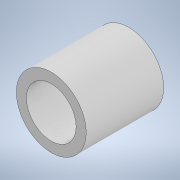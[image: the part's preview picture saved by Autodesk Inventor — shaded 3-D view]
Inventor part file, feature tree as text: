
AUTODESK INVENTOR PART (.ipt)
format: ipt  version: 2020 (Build 240168000, 168)  size: 101,888 bytes
history: native  units: in
note: dims shown in document units (in); Inventor stores cm internally (conversion verified against a paired STEP export)
features: extrude x1
ambient origin geometry x8: Origin, YZ Plane, XZ Plane, XY Plane, X Axis, Y Axis, Z Axis, Center Point
bodies: Solid1 (feature_tree)
feature tree (1):
  extrude  "Extrude1"  [1 undecoded]
note: 1 required parameter value undecoded (feature->parameter linkage not recoverable at this tier; creation-order binding heuristic only, values carry confidence <= 0.55)
